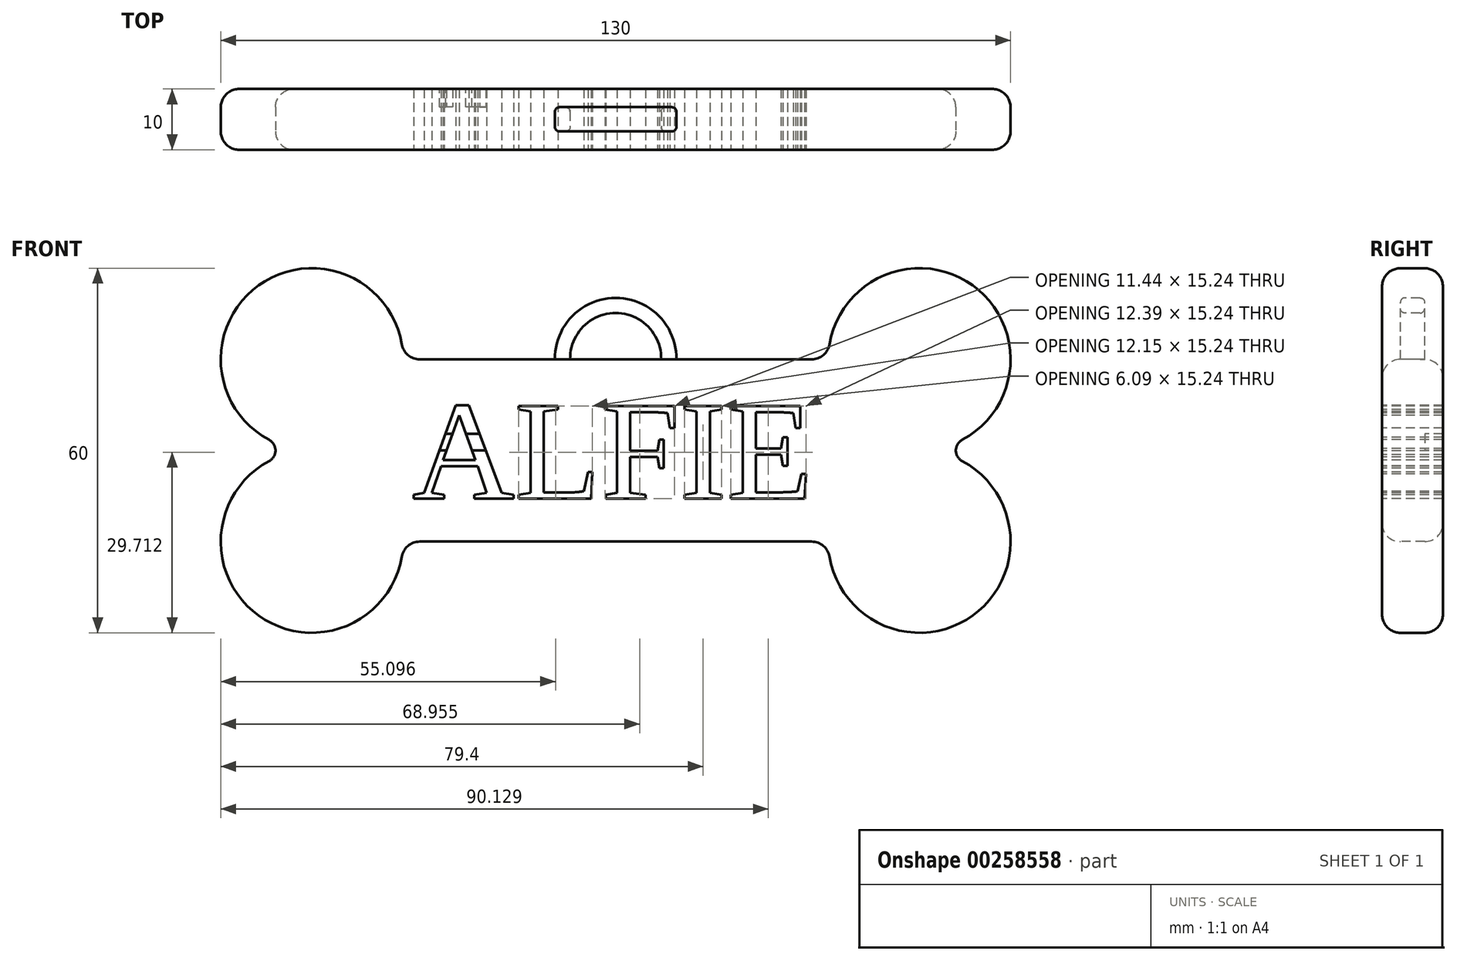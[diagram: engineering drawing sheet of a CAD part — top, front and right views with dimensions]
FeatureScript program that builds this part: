
annotation { "Feature Type Name" : "Feature", "Feature Type Description" : "" }
export const myFeature = defineFeature(function(context is Context, id is Id, definition is map)
    precondition{}
    {
        {
            var Q0;
            Q0=qCreatedBy(makeId("Front.planeOp"),FACE);
            var sketch = newSketch(context, id + "F0", { "sketchPlane" : qUnion([Q0])});
            skLineSegment(sketch, "E0.bottom", {"start": v(-32.25, 15) * mm, "end": v(32.25, 15) * mm});
            skPoint(sketch, "E0.middle", {"position": v(0, 0) * mm});
            skArc(sketch, "E1", {"start": v(-35.2, 17.5) * mm, "mid": v(-58.77, 27.17) * mm, "end": v(-57.06, 1.76) * mm});
            skArc(sketch, "E2", {"start": v(-57.06, -1.76) * mm, "mid": v(-58.77, -27.17) * mm, "end": v(-35.2, -17.5) * mm});
            skArc(sketch, "E3", {"start": v(57.06, 1.76) * mm, "mid": v(58.77, 27.17) * mm, "end": v(35.2, 17.5) * mm});
            skArc(sketch, "E4", {"start": v(35.2, -17.5) * mm, "mid": v(58.77, -27.17) * mm, "end": v(57.06, -1.76) * mm});
            skLineSegment(sketch, "E5", {"start": v(-32.25, -15) * mm, "end": v(32.25, -15) * mm});
            skPoint(sketch, "E6.visualSharp", {"position": v(-35, 15) * mm});
            skArc(sketch, "E6.filletArc", {"start": v(-35.2, 17.5) * mm, "mid": v(-34.19, 15.7) * mm, "end": v(-32.25, 15) * mm});
            skPoint(sketch, "E7.visualSharp", {"position": v(-35, -15) * mm});
            skArc(sketch, "E7.filletArc", {"start": v(-32.25, -15) * mm, "mid": v(-34.19, -15.7) * mm, "end": v(-35.2, -17.5) * mm});
            skPoint(sketch, "E8.visualSharp", {"position": v(35, -15) * mm});
            skArc(sketch, "E8.filletArc", {"start": v(35.2, -17.5) * mm, "mid": v(34.19, -15.7) * mm, "end": v(32.25, -15) * mm});
            skPoint(sketch, "E9.visualSharp", {"position": v(35, 15) * mm});
            skArc(sketch, "E9.filletArc", {"start": v(32.25, 15) * mm, "mid": v(34.19, 15.7) * mm, "end": v(35.2, 17.5) * mm});
            skPoint(sketch, "E10.visualSharp", {"position": v(-50, 0) * mm});
            skArc(sketch, "E10.filletArc", {"start": v(-57.06, -1.76) * mm, "mid": v(-56, 0) * mm, "end": v(-57.06, 1.76) * mm});
            skPoint(sketch, "E11.visualSharp", {"position": v(50, 0) * mm});
            skArc(sketch, "E11.filletArc", {"start": v(57.06, 1.76) * mm, "mid": v(56, 0) * mm, "end": v(57.06, -1.76) * mm});
            skSolve(sketch);
        }
        {
            var Q0;
            Q0=makeQuery(id+"F0.imprint","IMPRINT",FACE,{"disambiguationData":[TD([[makeQuery(id+"F0.imprint","IMPRINT",EDGE,{"derivedFrom":sQuery(id+"F0.wireOp",EDGE,"E0.bottom")}),-1.0]])]});
            extrude(context, id + "F1", {"entities" : qUnion([Q0]), "oppositeDirection" : true, "depth" : 10 * mm});
        }
        {
            var Q0;
            Q0=qCreatedBy(makeId("Front.planeOp"),FACE);
            var sketch = newSketch(context, id + "F2", { "sketchPlane" : qUnion([Q0])});
            skText(sketch, "E12", { "text": "ALFIE", "fontName": "Tinos-Regular.ttf"});
            const initialGuessF2  = {"E12": [-0.03346, -0.00791, 1, 0, 0.01676]};
            skSetInitialGuess(sketch, initialGuessF2);
            skSolve(sketch);
        }
        {
            var Q0;
            Q0=makeQuery(id+"F1.opExtrude","CAP_EDGE",EDGE,{"disambiguationData":[OSD([sQuery(id+"F0.wireOp",EDGE,"E3")])],"isStart":true});
            var Q1;
            Q1=makeQuery(id+"F1.opExtrude","CAP_EDGE",EDGE,{"disambiguationData":[OSD([sQuery(id+"F0.wireOp",EDGE,"E3")])],"isStart":false});
            fillet(context, id + "F3", {"entities" : qUnion([Q0, Q1]), "radius" : 3 * mm, "tangentPropagation" : true, "allowEdgeOverflow" : false});
        }
        {
            var Q0;
            Q0 = qSketchRegion(id + "F2", true);
            extrude(context, id + "F4", {"entities" : qUnion([Q0]), "operationType" : NewBodyOperationType.REMOVE, "oppositeDirection" : true, "depth" : 25 * mm});
        }
        {
            var Q0;
            {var subQ0=sQuery(id+"F0.wireOp",EDGE,"E1");var subQ1=sQuery(id+"F0.wireOp",EDGE,"E7.filletArc");var subQ2=sQuery(id+"F0.wireOp",EDGE,"E11.filletArc");var subQ3=sQuery(id+"F0.wireOp",EDGE,"E4");var subQ4=sQuery(id+"F0.wireOp",EDGE,"E3");var subQ5=sQuery(id+"F0.wireOp",EDGE,"E5");var subQ6=sQuery(id+"F0.wireOp",EDGE,"E10.filletArc");var subQ7=sQuery(id+"F0.wireOp",EDGE,"E2");var subQ8=sQuery(id+"F0.wireOp",EDGE,"E0.bottom");var subQ9=sQuery(id+"F0.wireOp",EDGE,"E9.filletArc");var subQ10=sQuery(id+"F0.wireOp",EDGE,"E8.filletArc");var subQ11=sQuery(id+"F0.wireOp",EDGE,"E6.filletArc");Q0=makeQuery(id+"F4.boolean.opBoolean","SPLIT",FACE,{"disambiguationData":[TD([makeQuery(id+"F4.opExtrude","SWEPT_FACE",FACE,{"disambiguationData":[OSD([sQuery(id+"F2.wireOp",EDGE,"E12.sketch_text.stroke-0")])]})])],"derivedFrom":makeQuery(id+"F1.opExtrude","CAP_FACE",FACE,{"disambiguationData":[OSD([subQ8,subQ0,subQ7,subQ4,subQ3,subQ5,subQ11,subQ1,subQ10,subQ9,subQ6,subQ2])],"isStart":true})});}
            var sketch = newSketch(context, id + "F5", { "sketchPlane" : qUnion([Q0])});
            skArc(sketch, "E13", {"start": v(8.25, 9.47) * mm, "mid": v(-1.13, 25.06) * mm, "end": v(-6.77, 7.76) * mm});
            skArc(sketch, "E14", {"start": v(4.65, 9.24) * mm, "mid": v(0.13, 22.62) * mm, "end": v(-4.85, 9.4) * mm});
            skSolve(sketch);
        }
        {
            var Q0;
            {var subQ0=sQuery(id+"F5.wireOp",EDGE,"E13");var subQ1=sQuery(id+"F0.wireOp",EDGE,"E0.bottom");var subQ2=makeQuery(id+"F3.opFillet","BLEND_EDGE",EDGE,{"blendedFrom":[makeQuery(id+"F1.opExtrude","CAP_EDGE",EDGE,{"disambiguationData":[OSD([subQ1])],"isStart":true}),makeQuery(id+"F1.opExtrude","CAP_FACE",FACE,{"disambiguationData":[OSD([subQ1,sQuery(id+"F0.wireOp",EDGE,"E1"),sQuery(id+"F0.wireOp",EDGE,"E2"),sQuery(id+"F0.wireOp",EDGE,"E3"),sQuery(id+"F0.wireOp",EDGE,"E4"),sQuery(id+"F0.wireOp",EDGE,"E5"),sQuery(id+"F0.wireOp",EDGE,"E6.filletArc"),sQuery(id+"F0.wireOp",EDGE,"E7.filletArc"),sQuery(id+"F0.wireOp",EDGE,"E8.filletArc"),sQuery(id+"F0.wireOp",EDGE,"E9.filletArc"),sQuery(id+"F0.wireOp",EDGE,"E10.filletArc"),sQuery(id+"F0.wireOp",EDGE,"E11.filletArc")])],"isStart":true})],"blendedInto":[makeQuery(id+"F1.opExtrude","CAP_FACE",FACE,{"disambiguationData":[OSD([subQ1,sQuery(id+"F0.wireOp",EDGE,"E1"),sQuery(id+"F0.wireOp",EDGE,"E2"),sQuery(id+"F0.wireOp",EDGE,"E3"),sQuery(id+"F0.wireOp",EDGE,"E4"),sQuery(id+"F0.wireOp",EDGE,"E5"),sQuery(id+"F0.wireOp",EDGE,"E6.filletArc"),sQuery(id+"F0.wireOp",EDGE,"E7.filletArc"),sQuery(id+"F0.wireOp",EDGE,"E8.filletArc"),sQuery(id+"F0.wireOp",EDGE,"E9.filletArc"),sQuery(id+"F0.wireOp",EDGE,"E10.filletArc"),sQuery(id+"F0.wireOp",EDGE,"E11.filletArc")])],"isStart":true})]});var subQ3=makeQuery(id+"F5.imprint","INTERSECT",VERTEX,{"disambiguationData":[OD(0.0)],"derivedFrom":[subQ2,subQ0]});Q0=makeQuery(id+"F5.imprint","IMPRINT",FACE,{"disambiguationData":[TD([[makeQuery(id+"F5.imprint","IMPRINT",EDGE,{"disambiguationData":[TD([[subQ3,1.0]])],"derivedFrom":subQ0}),1.0]])]});}
            extrude(context, id + "F6", {"entities" : qUnion([Q0]), "operationType" : NewBodyOperationType.ADD, "oppositeDirection" : true, "depth" : 7 * mm, "hasSecondDirection" : true, "secondDirectionOppositeDirection" : true, "secondDirectionDepth" : 3 * mm});
        }
        {
            var Q0;
            Q0=makeQuery(id+"F6.opExtrude","CAP_EDGE",EDGE,{"disambiguationData":[OSD([sQuery(id+"F5.wireOp",EDGE,"E13")])],"isStart":true});
            var Q1;
            Q1=makeQuery(id+"F6.opExtrude","CAP_EDGE",EDGE,{"disambiguationData":[OSD([sQuery(id+"F5.wireOp",EDGE,"E14")])],"isStart":true});
            var Q2;
            Q2=makeQuery(id+"F6.opExtrude","CAP_EDGE",EDGE,{"disambiguationData":[OSD([sQuery(id+"F5.wireOp",EDGE,"E13")])],"isStart":false});
            var Q3;
            Q3=makeQuery(id+"F6.opExtrude","CAP_EDGE",EDGE,{"disambiguationData":[OSD([sQuery(id+"F5.wireOp",EDGE,"E14")])],"isStart":false});
            fillet(context, id + "F7", {"entities" : qUnion([Q0, Q1, Q2, Q3]), "radius" : .75 * mm, "tangentPropagation" : true, "allowEdgeOverflow" : false});
        }
        {
            var Q0;
            {var subQ0=sQuery(id+"F0.wireOp",EDGE,"E9.filletArc");var subQ1=sQuery(id+"F0.wireOp",EDGE,"E3");var subQ2=sQuery(id+"F0.wireOp",EDGE,"E1");var subQ3=sQuery(id+"F0.wireOp",EDGE,"E6.filletArc");var subQ4=sQuery(id+"F0.wireOp",EDGE,"E11.filletArc");var subQ5=sQuery(id+"F0.wireOp",EDGE,"E5");var subQ6=sQuery(id+"F0.wireOp",EDGE,"E10.filletArc");var subQ7=sQuery(id+"F0.wireOp",EDGE,"E2");var subQ8=sQuery(id+"F0.wireOp",EDGE,"E4");var subQ9=sQuery(id+"F0.wireOp",EDGE,"E0.bottom");var subQ10=sQuery(id+"F0.wireOp",EDGE,"E8.filletArc");var subQ11=sQuery(id+"F0.wireOp",EDGE,"E7.filletArc");Q0=makeQuery(id+"F4.boolean.opBoolean","SPLIT",FACE,{"disambiguationData":[TD([makeQuery(id+"F4.opExtrude","SWEPT_FACE",FACE,{"disambiguationData":[OSD([sQuery(id+"F2.wireOp",EDGE,"E12.sketch_text.stroke-0")])]})])],"derivedFrom":makeQuery(id+"F1.opExtrude","CAP_FACE",FACE,{"disambiguationData":[OSD([subQ9,subQ2,subQ7,subQ1,subQ8,subQ5,subQ3,subQ11,subQ10,subQ0,subQ6,subQ4])],"isStart":false})});}
            var sketch = newSketch(context, id + "F8", { "sketchPlane" : qUnion([Q0])});
            skLineSegment(sketch, "E15.bottom", {"start": v(20.47, 2.75) * mm, "end": v(30.4, 2.75) * mm});
            skLineSegment(sketch, "E15.top", {"start": v(20.47, 0) * mm, "end": v(30.4, 0) * mm});
            skLineSegment(sketch, "E15.left", {"start": v(20.47, 2.75) * mm, "end": v(20.47, 0) * mm});
            skLineSegment(sketch, "E15.right", {"start": v(30.4, 2.75) * mm, "end": v(30.4, 0) * mm});
            skSolve(sketch);
        }
        {
            var Q0;
            Q0 = qSketchRegion(id + "F8", true);
            extrude(context, id + "F9", {"entities" : qUnion([Q0]), "operationType" : NewBodyOperationType.ADD, "oppositeDirection" : true, "depth" : 3 * mm});
        }
    });
